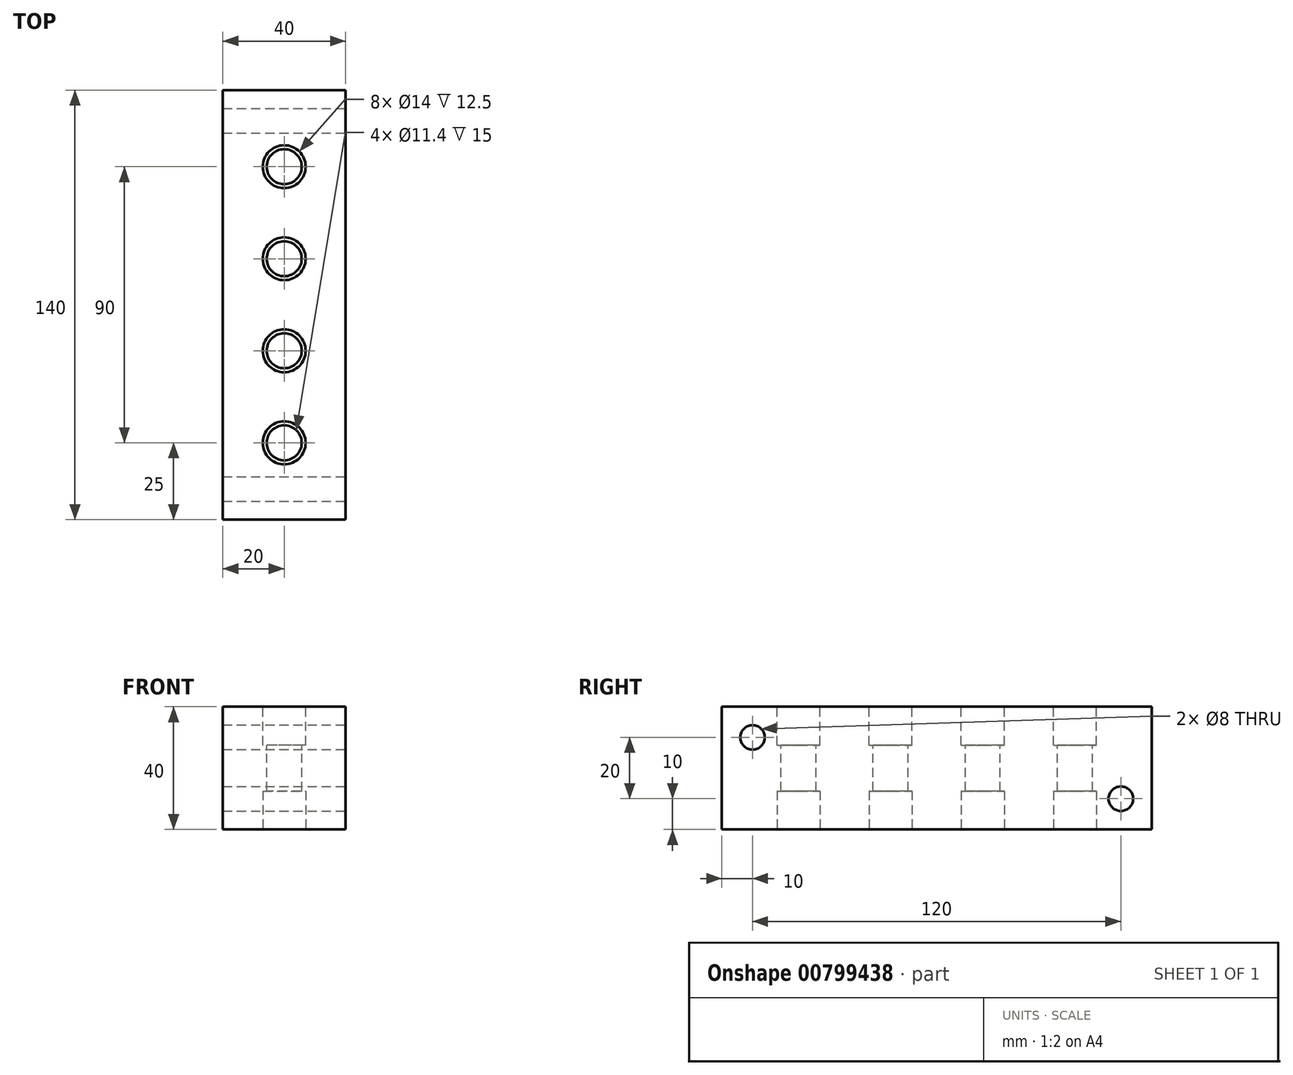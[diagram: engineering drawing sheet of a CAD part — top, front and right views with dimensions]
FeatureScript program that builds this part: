
annotation { "Feature Type Name" : "Feature", "Feature Type Description" : "" }
export const myFeature = defineFeature(function(context is Context, id is Id, definition is map)
    precondition{}
    {
        {
            var Q0;
            Q0=qCreatedBy(makeId("Front.planeOp"),FACE);
            var sketch = newSketch(context, id + "F0", { "sketchPlane" : qUnion([Q0])});
            skLineSegment(sketch, "E0.bottom", {"start": v(20, 20) * mm, "end": v(-20, 20) * mm});
            skLineSegment(sketch, "E0.top", {"start": v(20, -20) * mm, "end": v(-20, -20) * mm});
            skLineSegment(sketch, "E0.left", {"start": v(20, 20) * mm, "end": v(20, -20) * mm});
            skLineSegment(sketch, "E0.right", {"start": v(-20, 20) * mm, "end": v(-20, -20) * mm});
            skPoint(sketch, "E0.middle", {"position": v(0, 0) * mm});
            skSolve(sketch);
        }
        {
            var Q0;
            Q0=makeQuery(id+"F0.imprint","IMPRINT",FACE,{"disambiguationData":[TD([[makeQuery(id+"F0.imprint","IMPRINT",EDGE,{"derivedFrom":sQuery(id+"F0.wireOp",EDGE,"E0.bottom")}),1.0]])]});
            extrude(context, id + "F1", {"entities" : qUnion([Q0]), "depth" : 140 * mm, "offsetDistance" : 25 * mm});
        }
        {
            var Q0;
            Q0=makeQuery(id+"F1.opExtrude","SWEPT_FACE",FACE,{"disambiguationData":[OSD([sQuery(id+"F0.wireOp",EDGE,"E0.bottom")])]});
            var sketch = newSketch(context, id + "F2", { "sketchPlane" : qUnion([Q0])});
            skLineSegment(sketch, "E1", {"start": v(0, -140) * mm, "end": v(0, 0) * mm, "construction": true});
            skCircle(sketch, "E2", {"center": v(0, -25) * mm, "radius": 5.7 * mm});
            skCircle(sketch, "E3", {"center": v(0, -55) * mm, "radius": 5.7 * mm});
            skCircle(sketch, "E4", {"center": v(0, -85) * mm, "radius": 5.7 * mm});
            skCircle(sketch, "E5", {"center": v(0, -115) * mm, "radius": 5.7 * mm});
            skSolve(sketch);
        }
        {
            var Q0;
            Q0=makeQuery(id+"F2.imprint","IMPRINT",FACE,{"disambiguationData":[TD([[makeQuery(id+"F2.imprint","IMPRINT",EDGE,{"derivedFrom":sQuery(id+"F2.wireOp",EDGE,"E3")}),1.0]])]});
            var Q1;
            Q1=makeQuery(id+"F2.imprint","IMPRINT",FACE,{"disambiguationData":[TD([[makeQuery(id+"F2.imprint","IMPRINT",EDGE,{"derivedFrom":sQuery(id+"F2.wireOp",EDGE,"E4")}),1.0]])]});
            var Q2;
            Q2=makeQuery(id+"F2.imprint","IMPRINT",FACE,{"disambiguationData":[TD([[makeQuery(id+"F2.imprint","IMPRINT",EDGE,{"derivedFrom":sQuery(id+"F2.wireOp",EDGE,"E5")}),1.0]])]});
            var Q3;
            Q3=makeQuery(id+"F2.imprint","IMPRINT",FACE,{"disambiguationData":[TD([[makeQuery(id+"F2.imprint","IMPRINT",EDGE,{"derivedFrom":sQuery(id+"F2.wireOp",EDGE,"E2")}),1.0]])]});
            extrude(context, id + "F3", {"entities" : qUnion([Q0, Q1, Q2, Q3]), "operationType" : NewBodyOperationType.REMOVE, "oppositeDirection" : true, "depth" : 40 * mm, "offsetDistance" : 25 * mm});
        }
        {
            var Q0;
            Q0=makeQuery(id+"F1.opExtrude","SWEPT_FACE",FACE,{"disambiguationData":[OSD([sQuery(id+"F0.wireOp",EDGE,"E0.left")])]});
            var sketch = newSketch(context, id + "F4", { "sketchPlane" : qUnion([Q0])});
            skCircle(sketch, "E6", {"center": v(-130, 10) * mm, "radius": 4 * mm});
            skCircle(sketch, "E7", {"center": v(-10, -10) * mm, "radius": 4 * mm});
            skSolve(sketch);
        }
        {
            var Q0;
            Q0 = qSketchRegion(id + "F4", true);
            extrude(context, id + "F5", {"entities" : qUnion([Q0]), "operationType" : NewBodyOperationType.REMOVE, "oppositeDirection" : true, "depth" : 40 * mm, "offsetDistance" : 25 * mm});
        }
        {
            var Q0;
            Q0=makeQuery(id+"F1.opExtrude","SWEPT_FACE",FACE,{"disambiguationData":[OSD([sQuery(id+"F0.wireOp",EDGE,"E0.top")])]});
            var sketch = newSketch(context, id + "F6", { "sketchPlane" : qUnion([Q0])});
            skCircle(sketch, "E8", {"center": v(0, 115) * mm, "radius": 7 * mm});
            skCircle(sketch, "E9", {"center": v(0, 85) * mm, "radius": 7 * mm});
            skCircle(sketch, "E10", {"center": v(0, 55) * mm, "radius": 7 * mm});
            skCircle(sketch, "E11", {"center": v(0, 25) * mm, "radius": 7 * mm});
            skSolve(sketch);
        }
        {
            var Q0;
            Q0=makeQuery(id+"F6.imprint","IMPRINT",FACE,{"disambiguationData":[TD([[makeQuery(id+"F6.imprint","IMPRINT",EDGE,{"derivedFrom":sQuery(id+"F6.wireOp",EDGE,"E8")}),1.0]])]});
            var Q1;
            Q1=makeQuery(id+"F6.imprint","IMPRINT",FACE,{"disambiguationData":[TD([[makeQuery(id+"F6.imprint","IMPRINT",EDGE,{"derivedFrom":sQuery(id+"F6.wireOp",EDGE,"E9")}),1.0]])]});
            var Q2;
            Q2=makeQuery(id+"F6.imprint","IMPRINT",FACE,{"disambiguationData":[TD([[makeQuery(id+"F6.imprint","IMPRINT",EDGE,{"derivedFrom":sQuery(id+"F6.wireOp",EDGE,"E10")}),1.0]])]});
            var Q3;
            Q3=makeQuery(id+"F6.imprint","IMPRINT",FACE,{"disambiguationData":[TD([[makeQuery(id+"F6.imprint","IMPRINT",EDGE,{"derivedFrom":sQuery(id+"F6.wireOp",EDGE,"E11")}),1.0]])]});
            extrude(context, id + "F7", {"entities" : qUnion([Q0, Q1, Q2, Q3]), "operationType" : NewBodyOperationType.REMOVE, "oppositeDirection" : true, "depth" : 12.5 * mm, "offsetDistance" : 25 * mm});
        }
        {
            var Q0;
            Q0=makeQuery(id+"F1.opExtrude","SWEPT_FACE",FACE,{"disambiguationData":[OSD([sQuery(id+"F0.wireOp",EDGE,"E0.bottom")])]});
            var sketch = newSketch(context, id + "F8", { "sketchPlane" : qUnion([Q0])});
            skCircle(sketch, "E12", {"center": v(0, -25) * mm, "radius": 7 * mm});
            skCircle(sketch, "E13", {"center": v(0, -55) * mm, "radius": 7 * mm});
            skCircle(sketch, "E14", {"center": v(0, -85) * mm, "radius": 7 * mm});
            skCircle(sketch, "E15", {"center": v(0, -115) * mm, "radius": 7 * mm});
            skSolve(sketch);
        }
        {
            var Q0;
            Q0=makeQuery(id+"F8.imprint","IMPRINT",FACE,{"disambiguationData":[TD([[makeQuery(id+"F8.imprint","IMPRINT",EDGE,{"derivedFrom":sQuery(id+"F8.wireOp",EDGE,"E12")}),1.0]])]});
            var Q1;
            Q1=makeQuery(id+"F8.imprint","IMPRINT",FACE,{"disambiguationData":[TD([[makeQuery(id+"F8.imprint","IMPRINT",EDGE,{"derivedFrom":sQuery(id+"F8.wireOp",EDGE,"E13")}),1.0]])]});
            var Q2;
            Q2=makeQuery(id+"F8.imprint","IMPRINT",FACE,{"disambiguationData":[TD([[makeQuery(id+"F8.imprint","IMPRINT",EDGE,{"derivedFrom":sQuery(id+"F8.wireOp",EDGE,"E14")}),1.0]])]});
            var Q3;
            Q3=makeQuery(id+"F8.imprint","IMPRINT",FACE,{"disambiguationData":[TD([[makeQuery(id+"F8.imprint","IMPRINT",EDGE,{"derivedFrom":sQuery(id+"F8.wireOp",EDGE,"E15")}),1.0]])]});
            extrude(context, id + "F9", {"entities" : qUnion([Q0, Q1, Q2, Q3]), "operationType" : NewBodyOperationType.REMOVE, "oppositeDirection" : true, "depth" : 12.5 * mm, "offsetDistance" : 25 * mm});
        }
    });
